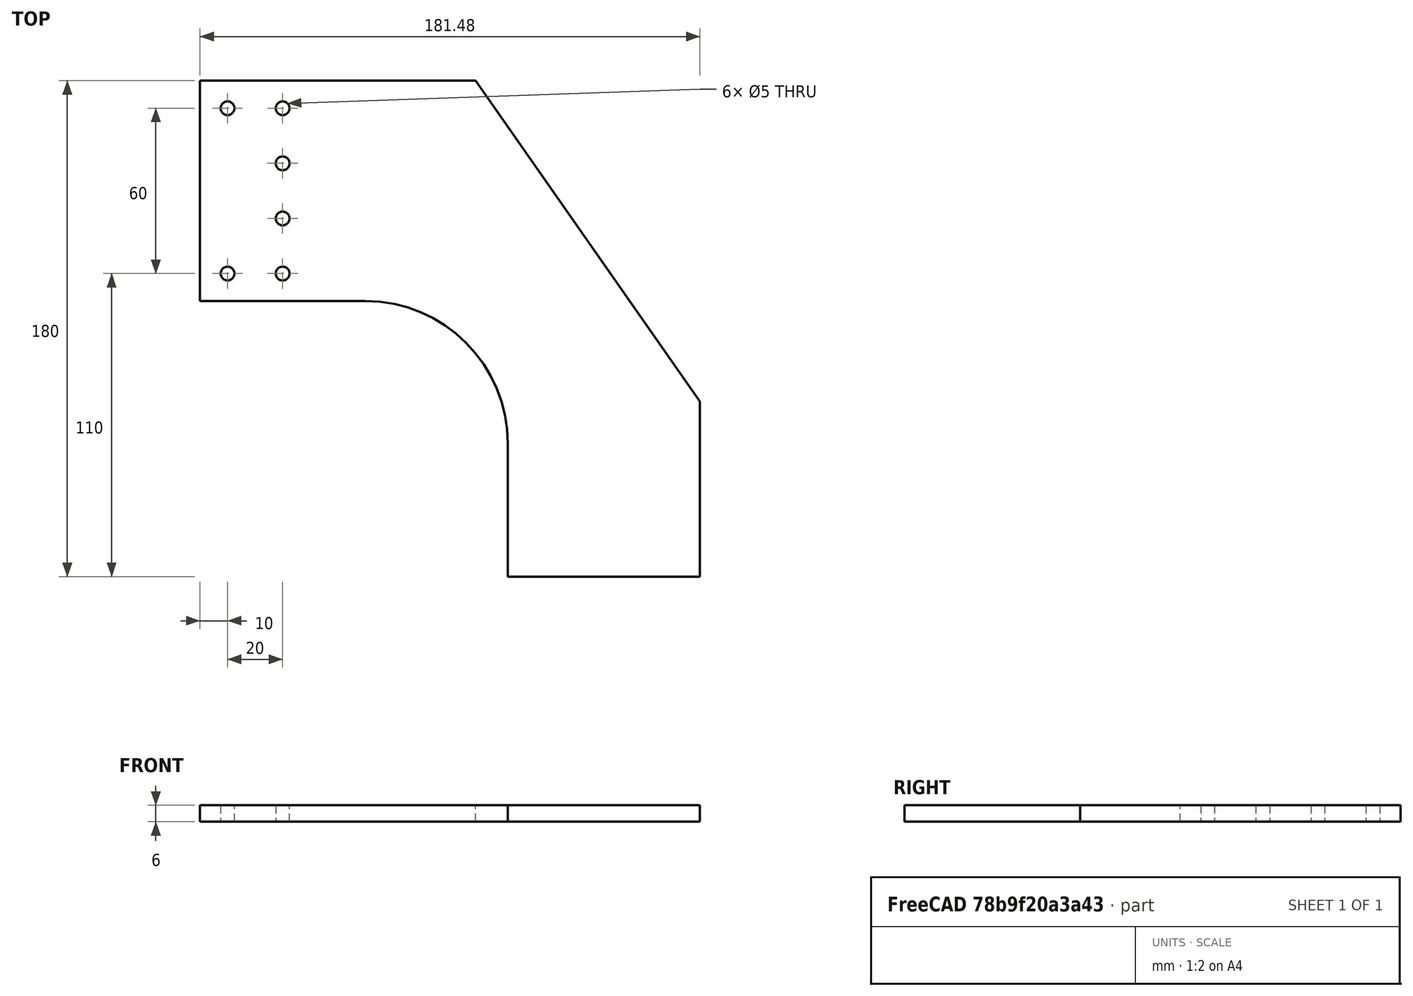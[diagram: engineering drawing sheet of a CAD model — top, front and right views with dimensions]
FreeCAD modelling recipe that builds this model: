
FCSTD DOCUMENT  (FreeCAD 0.20R29177 (Git))
Label: EndPlates
License: All rights reserved
LicenseURL: http://en.wikipedia.org/wiki/All_rights_reserved
objects: Sketcher::SketchObject×2, PartDesign::Pad×1, PartDesign::CoordinateSystem×1, PartDesign::Body×1
note: 6 computed .brp shape members not serialized (recipe doc carries the construction recipe); baked Part::Feature solids carry a one-line shape summary decoded from their .brp

FEATURE [Sketcher::SketchObject] Sketch
  FullyConstrained = false
  MapMode = 5
  Support = -> [XY_Plane]
  sketch-geometry (14):
    g0: LineSegment StartX=181.481 StartY=0 StartZ=0 EndX=181.481 EndY=63.6335 EndZ=0
    g1: LineSegment StartX=181.481 StartY=63.6335 StartZ=0 EndX=100 EndY=180 EndZ=0
    g2: LineSegment StartX=100 StartY=180 StartZ=0 EndX=0 EndY=180 EndZ=0
    g3: LineSegment StartX=0 StartY=180 StartZ=0 EndX=0 EndY=100 EndZ=0
    g4: LineSegment StartX=0 StartY=100 StartZ=0 EndX=60 EndY=100 EndZ=0
    g5: LineSegment StartX=111.775 StartY=48.2248 StartZ=0 EndX=111.775 EndY=0 EndZ=0
    g6: ArcOfCircle CenterX=60 CenterY=48.2248 CenterZ=0 NormalX=0 NormalY=0 NormalZ=1 AngleXU=0 Radius=51.7752 StartAngle=0 EndAngle=1.5708
    g7: Circle CenterX=10 CenterY=170 CenterZ=0 NormalX=0 NormalY=0 NormalZ=1 AngleXU=0 Radius=2.5
    g8: Circle CenterX=30 CenterY=170 CenterZ=0 NormalX=0 NormalY=0 NormalZ=1 AngleXU=0 Radius=2.5
    g9: Circle CenterX=30 CenterY=150 CenterZ=0 NormalX=0 NormalY=0 NormalZ=1 AngleXU=0 Radius=2.5
    g10: Circle CenterX=30 CenterY=130 CenterZ=0 NormalX=0 NormalY=0 NormalZ=1 AngleXU=0 Radius=2.5
    g11: Circle CenterX=30 CenterY=110 CenterZ=0 NormalX=0 NormalY=0 NormalZ=1 AngleXU=0 Radius=2.5
    g12: Circle CenterX=10 CenterY=110 CenterZ=0 NormalX=0 NormalY=0 NormalZ=1 AngleXU=0 Radius=2.5
    g13: LineSegment StartX=111.775 StartY=0 StartZ=0 EndX=181.481 EndY=0 EndZ=0
  constraints (39):
    c: PointOnObject(g0,g-1)
    c: Vertical(g0)
    c: Coincident(g0,g1)
    c: Coincident(g1,g2)
    c: PointOnObject(g2,g-2)
    c: Horizontal(g2)
    c: Coincident(g2,g3)
    c: PointOnObject(g3,g-2)
    c: Coincident(g3,g4)
    c: Horizontal(g4)
    c: Angle(g1,g0) = 2.53073
    c: DistanceX(g2,g2) = 100
    c: DistanceY(g3,g3) = 80
    c: Vertical(g5)
    c: Tangent(g4,g6) = 1.5708
    c: Tangent(g5,g6) = 1.5708
    c: Diameter(g7) = 5
    c: Diameter(g12) = 5
    c: Diameter(g11) = 5
    c: Diameter(g10) = 5
    c: Diameter(g9) = 5
    c: Diameter(g8) = 5
    c: DistanceX(g2,g7) = 10
    c: DistanceX(g7,g8) = 20
    c: Vertical(g9,g8)
    c: Vertical(g10,g9)
    c: Vertical(g11,g10)
    c: Horizontal(g12,g11)
    c: Vertical(g12,g7)
    c: DistanceY(g11,g10) = 20
    c: DistanceY(g10,g9) = 20
    c: DistanceY(g9,g8) = 20
    c: Horizontal(g7,g8)
    c: DistanceY(g7,g2) = 10
    c: DistanceX(g4,g4) = 60
    c: DistanceY(g5,g1) = 180
    c: Coincident(g13,g5)
    c: Coincident(g13,g0)
    c: Horizontal(g13)
FEATURE [PartDesign::Pad] Pad
  Direction = (0,0,1)
  Length = 6
  Length2 = 10
  Profile = -> Sketch
  ReferenceAxis = -> Sketch [N_Axis]
  Type = 0
FEATURE [PartDesign::CoordinateSystem] LCS_1_LH
  AttacherType = Attacher::AttachEngine3D
  MapMode = 11
  Placement = pos=(30,170,6) rot=(0,0,1;1.5708rad)
  Support = -> [Pad]
FEATURE [Sketcher::SketchObject] Sketch001
  FullyConstrained = true
  MapMode = 5
  Support = -> [XY_Plane]
FEATURE [PartDesign::Body] Body
  Group = -> [Sketch,Pad,LCS_1_LH,Sketch001]
  Origin = -> Origin
  Tip = -> Pad
